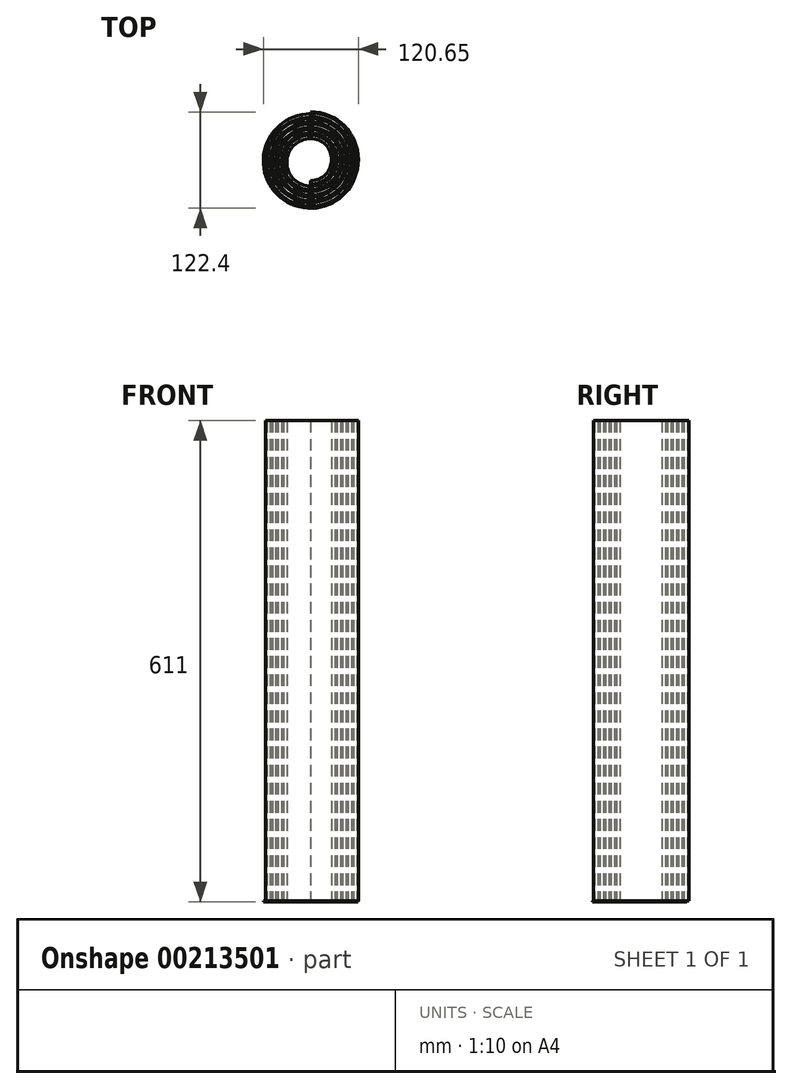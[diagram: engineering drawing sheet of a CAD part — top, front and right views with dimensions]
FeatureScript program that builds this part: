
annotation { "Feature Type Name" : "Feature", "Feature Type Description" : "" }
export const myFeature = defineFeature(function(context is Context, id is Id, definition is map)
    precondition{}
    {
        {
            var Q0;
            Q0=qCreatedBy(makeId("Top.planeOp"),FACE);
            var sketch = newSketch(context, id + "F0", { "sketchPlane" : qUnion([Q0])});
            skCircle(sketch, "E0", {"center": v(0, 0) * mm, "radius": 25 * mm, "construction": true});
            skLineSegment(sketch, "E1", {"start": v(0, 0) * mm, "end": v(0, -25) * mm, "construction": true});
            skLineSegment(sketch, "E2", {"start": v(0, -25) * mm, "end": v(0, -32) * mm, "construction": true});
            skLineSegment(sketch, "E3", {"start": v(0, -32) * mm, "end": v(0, -39) * mm, "construction": true});
            skLineSegment(sketch, "E4", {"start": v(0, -39) * mm, "end": v(0, -46) * mm, "construction": true});
            skLineSegment(sketch, "E5", {"start": v(0, -46) * mm, "end": v(0, -53) * mm, "construction": true});
            skLineSegment(sketch, "E6", {"start": v(0, -53) * mm, "end": v(0, -60) * mm, "construction": true});
            skCircle(sketch, "E7", {"center": v(0, 0) * mm, "radius": 60 * mm, "construction": true});
            skLineSegment(sketch, "E8", {"start": v(0, 0) * mm, "end": v(0, 21.5) * mm, "construction": true});
            skLineSegment(sketch, "E9", {"start": v(0, 21.5) * mm, "end": v(0, 28.5) * mm, "construction": true});
            skLineSegment(sketch, "E10", {"start": v(0, 28.5) * mm, "end": v(0, 35.5) * mm, "construction": true});
            skLineSegment(sketch, "E11", {"start": v(0, 35.5) * mm, "end": v(0, 42.5) * mm, "construction": true});
            skLineSegment(sketch, "E12", {"start": v(0, 42.5) * mm, "end": v(0, 49.5) * mm, "construction": true});
            skLineSegment(sketch, "E13", {"start": v(0, 49.5) * mm, "end": v(0, 56.5) * mm, "construction": true});
            skLineSegment(sketch, "E14", {"start": v(0, 56.5) * mm, "end": v(0, 63.5) * mm, "construction": true});
            skPoint(sketch, "E15", {"position": v(0, 60) * mm});
            skPoint(sketch, "E16", {"position": v(0, 25) * mm});
            skLineSegment(sketch, "E17", {"start": v(0, -25) * mm, "end": v(-12.94, -25) * mm, "construction": true});
            skArc(sketch, "E18", {"start": v(0, -25) * mm, "mid": v(26.75, 1.75) * mm, "end": v(0, 28.5) * mm});
            skArc(sketch, "E19", {"start": v(0, 28.5) * mm, "mid": v(-30.25, -1.75) * mm, "end": v(0, -32) * mm});
            skArc(sketch, "E20", {"start": v(0, -32) * mm, "mid": v(33.75, 1.75) * mm, "end": v(0, 35.5) * mm});
            skArc(sketch, "E21", {"start": v(0, 35.5) * mm, "mid": v(-37.25, -1.75) * mm, "end": v(0, -39) * mm});
            skArc(sketch, "E22", {"start": v(0, -39) * mm, "mid": v(40.75, 1.75) * mm, "end": v(0, 42.5) * mm});
            skArc(sketch, "E23", {"start": v(0, 42.5) * mm, "mid": v(-44.25, -1.75) * mm, "end": v(0, -46) * mm});
            skArc(sketch, "E24", {"start": v(0, -46) * mm, "mid": v(47.75, 1.75) * mm, "end": v(0, 49.5) * mm});
            skArc(sketch, "E25", {"start": v(0, 49.5) * mm, "mid": v(-51.25, -1.75) * mm, "end": v(0, -53) * mm});
            skArc(sketch, "E26", {"start": v(0, -53) * mm, "mid": v(54.75, 1.75) * mm, "end": v(0, 56.5) * mm});
            skArc(sketch, "E27.0", {"start": v(0, -58.9) * mm, "mid": v(60.65, 1.75) * mm, "end": v(0, 62.4) * mm});
            skArc(sketch, "E27.1", {"start": v(0, 55.4) * mm, "mid": v(-57.15, -1.75) * mm, "end": v(0, -58.9) * mm});
            skArc(sketch, "E27.2", {"start": v(0, -51.9) * mm, "mid": v(53.65, 1.75) * mm, "end": v(0, 55.4) * mm});
            skArc(sketch, "E27.3", {"start": v(0, 48.4) * mm, "mid": v(-50.15, -1.75) * mm, "end": v(0, -51.9) * mm});
            skArc(sketch, "E27.4", {"start": v(0, -44.9) * mm, "mid": v(46.65, 1.75) * mm, "end": v(0, 48.4) * mm});
            skArc(sketch, "E27.5", {"start": v(0, -30.9) * mm, "mid": v(32.65, 1.75) * mm, "end": v(0, 34.4) * mm});
            skArc(sketch, "E27.6", {"start": v(0, 34.4) * mm, "mid": v(-36.15, -1.75) * mm, "end": v(0, -37.9) * mm});
            skArc(sketch, "E27.7", {"start": v(0, -37.9) * mm, "mid": v(39.65, 1.75) * mm, "end": v(0, 41.4) * mm});
            skArc(sketch, "E27.8", {"start": v(0, 41.4) * mm, "mid": v(-43.15, -1.75) * mm, "end": v(0, -44.9) * mm});
            skLineSegment(sketch, "E28", {"start": v(0, -30.9) * mm, "end": v(0, -25) * mm});
            skLineSegment(sketch, "E29", {"start": v(0, 56.5) * mm, "end": v(0, 62.4) * mm});
            skArc(sketch, "E30.0", {"start": v(0, -57.4) * mm, "mid": v(59.15, 1.75) * mm, "end": v(0, 60.9) * mm});
            skArc(sketch, "E30.1", {"start": v(0, 53.9) * mm, "mid": v(-55.65, -1.75) * mm, "end": v(0, -57.4) * mm});
            skArc(sketch, "E30.2", {"start": v(0, -50.4) * mm, "mid": v(52.15, 1.75) * mm, "end": v(0, 53.9) * mm});
            skArc(sketch, "E30.3", {"start": v(0, 46.9) * mm, "mid": v(-48.65, -1.75) * mm, "end": v(0, -50.4) * mm});
            skArc(sketch, "E30.4", {"start": v(0, -43.4) * mm, "mid": v(45.15, 1.75) * mm, "end": v(0, 46.9) * mm});
            skArc(sketch, "E30.5", {"start": v(0, -29.4) * mm, "mid": v(31.15, 1.75) * mm, "end": v(0, 32.9) * mm});
            skArc(sketch, "E30.6", {"start": v(0, 32.9) * mm, "mid": v(-34.65, -1.75) * mm, "end": v(0, -36.4) * mm});
            skArc(sketch, "E30.7", {"start": v(0, -36.4) * mm, "mid": v(38.15, 1.75) * mm, "end": v(0, 39.9) * mm});
            skArc(sketch, "E30.8", {"start": v(0, 39.9) * mm, "mid": v(-41.65, -1.75) * mm, "end": v(0, -43.4) * mm});
            skSolve(sketch);
        }
        {
            var Q0;
            {var subQ1=sQuery(id+"F0.wireOp",EDGE,"E18");Q0=makeQuery(id+"F0.imprint","IMPRINT",FACE,{"disambiguationData":[TD([[makeQuery(id+"F0.imprint","IMPRINT",EDGE,{"derivedFrom":subQ1}),-1.0]])]});}
            extrude(context, id + "F1", {"entities" : qUnion([Q0]), "depth" : 610 * mm});
        }
        {
            var Q0;
            Q0=qCreatedBy(makeId("Top.planeOp"),FACE);
            var sketch = newSketch(context, id + "F2", { "sketchPlane" : qUnion([Q0])});
            skCircle(sketch, "E31", {"center": v(0, 0) * mm, "radius": 60 * mm});
            skSolve(sketch);
        }
        {
            var Q0;
            {var subQ5=sQuery(id+"F0.wireOp",EDGE,"E27.0");Q0=makeQuery(id+"F0.imprint","IMPRINT",FACE,{"disambiguationData":[TD([[makeQuery(id+"F0.imprint","IMPRINT",EDGE,{"derivedFrom":subQ5}),1.0]])]});}
            var Q1;
            Q1=makeQuery(id+"F1.opExtrude","CAP_FACE",FACE,{"disambiguationData":[OSD([sQuery(id+"F0.wireOp",EDGE,"E18"),sQuery(id+"F0.wireOp",EDGE,"E19"),sQuery(id+"F0.wireOp",EDGE,"E20"),sQuery(id+"F0.wireOp",EDGE,"E21"),sQuery(id+"F0.wireOp",EDGE,"E22"),sQuery(id+"F0.wireOp",EDGE,"E23"),sQuery(id+"F0.wireOp",EDGE,"E24"),sQuery(id+"F0.wireOp",EDGE,"E25"),sQuery(id+"F0.wireOp",EDGE,"E26"),sQuery(id+"F0.wireOp",EDGE,"E28"),sQuery(id+"F0.wireOp",EDGE,"E29"),sQuery(id+"F0.wireOp",EDGE,"E30.0"),sQuery(id+"F0.wireOp",EDGE,"E30.1"),sQuery(id+"F0.wireOp",EDGE,"E30.2"),sQuery(id+"F0.wireOp",EDGE,"E30.3"),sQuery(id+"F0.wireOp",EDGE,"E30.4"),sQuery(id+"F0.wireOp",EDGE,"E30.5"),sQuery(id+"F0.wireOp",EDGE,"E30.6"),sQuery(id+"F0.wireOp",EDGE,"E30.7"),sQuery(id+"F0.wireOp",EDGE,"E30.8")])],"isStart":false});
            extrude(context, id + "F3", {"entities" : qUnion([Q0]), "endBound" : BoundingType.UP_TO_SURFACE, "endBoundEntityFace" : qUnion([Q1]), "depth" : 25 * mm});
        }
        {
            var Q0;
            Q0 = qSketchRegion(id + "F2", true);
            extrude(context, id + "F4", {"entities" : qUnion([Q0]), "oppositeDirection" : true, "depth" : 1 * mm});
        }
    });
